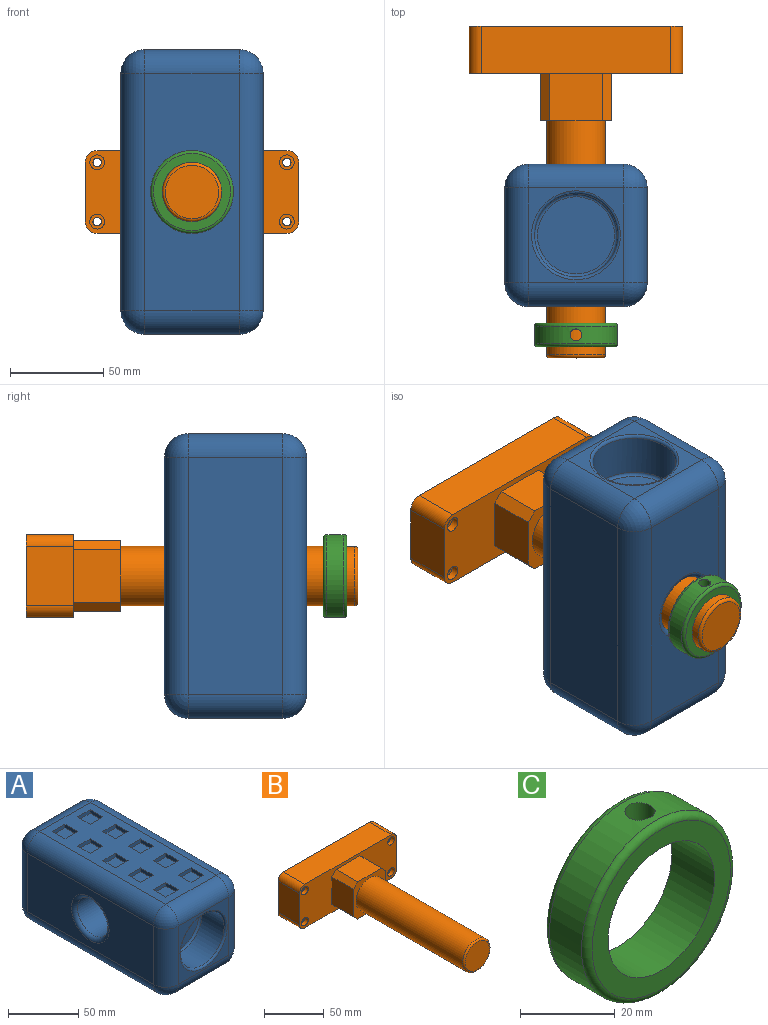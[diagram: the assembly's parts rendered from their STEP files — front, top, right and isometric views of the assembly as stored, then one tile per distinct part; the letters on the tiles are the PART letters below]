
ASSEMBLY  parts=3 mates=2
PART A: 87 faces, bbox 76.2x152.4x76.2 mm
  f0: plane 127x50.8mm, normal (0,0,1), area 4838.7mm2, adj f6,f10,f11,f12,f37,f38,f39,f40
  f1: plane 127x50.8mm, normal (0,0,-1), area 6451.6mm2, adj f14,f19,f22,f25
  f2: plane 127x50.8mm, normal (1,0,0), area 5311.5mm2, adj f11,f20,f21,f25,f36
  f3: plane 127x50.8mm, normal (-1,0,0), area 5311.5mm2, adj f6,f9,f13,f14,f35
  f4: plane 50.8x50.8mm, normal (0,-1,0), area 799.2mm2, adj f9,f10,f19,f20,f28
  f5: plane 50.8x50.8mm, normal (0,1,0), area 799.2mm2, adj f12,f13,f21,f22,f32
  f6: cylinder r=12.7mm len=127mm, axis (0,1,0), area 2533.5mm2, adj f0,f3,f7,f8
  f7: sphere r=12.7mm, area 253.4mm2, adj f6,f9,f10
  f8: sphere r=12.7mm, area 253.4mm2, adj f6,f12,f13
  f9: cylinder r=12.7mm len=50.8mm, axis (0,0,1), area 1013.4mm2, adj f3,f4,f7,f15
  f10: cylinder r=12.7mm len=50.8mm, axis (1,0,0), area 1013.4mm2, adj f0,f4,f7,f16
  f11: cylinder r=12.7mm len=127mm, axis (0,-1,0), area 2533.5mm2, adj f0,f2,f16,f17
  f12: cylinder r=12.7mm len=50.8mm, axis (-1,0,0), area 1013.4mm2, adj f0,f5,f8,f17
  f13: cylinder r=12.7mm len=50.8mm, axis (0,0,-1), area 1013.4mm2, adj f3,f5,f8,f18
  f14: cylinder r=12.7mm len=127mm, axis (0,-1,0), area 2533.5mm2, adj f1,f3,f15,f18
  f15: sphere r=12.7mm, area 253.4mm2, adj f9,f14,f19
  f16: sphere r=12.7mm, area 253.4mm2, adj f10,f11,f20
  f17: sphere r=12.7mm, area 253.4mm2, adj f11,f12,f21
  f18: sphere r=12.7mm, area 253.4mm2, adj f13,f14,f22
  f19: cylinder r=12.7mm len=50.8mm, axis (-1,0,0), area 1013.4mm2, adj f1,f4,f15,f23
  f20: cylinder r=12.7mm len=50.8mm, axis (0,0,-1), area 1013.4mm2, adj f2,f4,f16,f23
  f21: cylinder r=12.7mm len=50.8mm, axis (0,0,1), area 1013.4mm2, adj f2,f5,f17,f24
  f22: cylinder r=12.7mm len=50.8mm, axis (1,0,0), area 1013.4mm2, adj f1,f5,f18,f24
  f23: sphere r=12.7mm, area 253.4mm2, adj f19,f20,f25
  f24: sphere r=12.7mm, area 253.4mm2, adj f21,f22,f25
  f25: cylinder r=12.7mm len=127mm, axis (0,1,0), area 2533.5mm2, adj f1,f2,f23,f24
  f26: cylinder r=22.23mm len=44.45mm, axis (0,-1,0), area 3103.6mm2, adj f28,f29
  f27: plane 41.28x41.28mm, normal (0,-1,0), area 1338mm2, adj f29
  f28: torus R=23.81mm, axis (0,-1,0), area 357.3mm2, adj f4,f26
  f29: torus R=20.64mm, axis (0,-1,0), area 339.2mm2, adj f26,f27
  f30: cylinder r=22.23mm len=44.45mm, axis (0,1,0), area 3103.6mm2, adj f32,f33
  f31: plane 41.28x41.28mm, normal (0,1,0), area 1338mm2, adj f33
  f32: torus R=23.81mm, axis (0,-1,0), area 357.3mm2, adj f5,f30
  f33: torus R=20.64mm, axis (0,1,0), area 339.2mm2, adj f30,f31
  f34: cylinder r=15.88mm len=69.85mm, axis (1,0,0), area 6967.2mm2, adj f35,f36
  f35: torus R=19.05mm, axis (1,0,0), area 533.6mm2, adj f3,f34
  f36: torus R=19.05mm, axis (1,0,0), area 533.6mm2, adj f2,f34
  f37: plane 12.7x3.18mm, normal (0,-1,0), area 40.3mm2, adj f0,f38,f40,f41
  f38: plane 12.7x3.18mm, normal (1,0,0), area 40.3mm2, adj f0,f37,f39,f41
  f39: plane 12.7x3.18mm, normal (0,1,0), area 40.3mm2, adj f0,f38,f40,f41
  f40: plane 12.7x3.18mm, normal (-1,0,0), area 40.3mm2, adj f0,f37,f39,f41
  f41: plane 12.7x12.7mm, normal (0,0,1), area 161.3mm2, adj f37,f38,f39,f40
  f42: plane 12.7x3.18mm, normal (0,-1,0), area 40.3mm2, adj f0,f43,f45,f46
  f43: plane 12.7x3.18mm, normal (1,0,0), area 40.3mm2, adj f0,f42,f44,f46
  f44: plane 12.7x3.18mm, normal (0,1,0), area 40.3mm2, adj f0,f43,f45,f46
  f45: plane 12.7x3.18mm, normal (-1,0,0), area 40.3mm2, adj f0,f42,f44,f46
  f46: plane 12.7x12.7mm, normal (0,0,1), area 161.3mm2, adj f42,f43,f44,f45
  f47: plane 12.7x3.18mm, normal (0,-1,0), area 40.3mm2, adj f0,f48,f50,f51
  f48: plane 12.7x3.18mm, normal (1,0,0), area 40.3mm2, adj f0,f47,f49,f51
  f49: plane 12.7x3.18mm, normal (0,1,0), area 40.3mm2, adj f0,f48,f50,f51
  f50: plane 12.7x3.18mm, normal (-1,0,0), area 40.3mm2, adj f0,f47,f49,f51
  f51: plane 12.7x12.7mm, normal (0,0,1), area 161.3mm2, adj f47,f48,f49,f50
  f52: plane 12.7x3.18mm, normal (0,-1,0), area 40.3mm2, adj f0,f53,f55,f56
  f53: plane 12.7x3.18mm, normal (1,0,0), area 40.3mm2, adj f0,f52,f54,f56
  f54: plane 12.7x3.18mm, normal (0,1,0), area 40.3mm2, adj f0,f53,f55,f56
  f55: plane 12.7x3.18mm, normal (-1,0,0), area 40.3mm2, adj f0,f52,f54,f56
  f56: plane 12.7x12.7mm, normal (0,0,1), area 161.3mm2, adj f52,f53,f54,f55
  f57: plane 12.7x3.18mm, normal (0,-1,0), area 40.3mm2, adj f0,f58,f60,f61
  f58: plane 12.7x3.18mm, normal (1,0,0), area 40.3mm2, adj f0,f57,f59,f61
  f59: plane 12.7x3.18mm, normal (0,1,0), area 40.3mm2, adj f0,f58,f60,f61
  f60: plane 12.7x3.18mm, normal (-1,0,0), area 40.3mm2, adj f0,f57,f59,f61
  f61: plane 12.7x12.7mm, normal (0,0,1), area 161.3mm2, adj f57,f58,f59,f60
  f62: plane 12.7x3.18mm, normal (0,-1,0), area 40.3mm2, adj f0,f63,f65,f66
  f63: plane 12.7x3.18mm, normal (1,0,0), area 40.3mm2, adj f0,f62,f64,f66
  f64: plane 12.7x3.18mm, normal (0,1,0), area 40.3mm2, adj f0,f63,f65,f66
  f65: plane 12.7x3.18mm, normal (-1,0,0), area 40.3mm2, adj f0,f62,f64,f66
  f66: plane 12.7x12.7mm, normal (0,0,1), area 161.3mm2, adj f62,f63,f64,f65
  f67: plane 12.7x3.18mm, normal (0,-1,0), area 40.3mm2, adj f0,f68,f70,f71
  f68: plane 12.7x3.18mm, normal (1,0,0), area 40.3mm2, adj f0,f67,f69,f71
  f69: plane 12.7x3.18mm, normal (0,1,0), area 40.3mm2, adj f0,f68,f70,f71
  f70: plane 12.7x3.18mm, normal (-1,0,0), area 40.3mm2, adj f0,f67,f69,f71
  f71: plane 12.7x12.7mm, normal (0,0,1), area 161.3mm2, adj f67,f68,f69,f70
  f72: plane 12.7x3.18mm, normal (0,-1,0), area 40.3mm2, adj f0,f73,f75,f76
  f73: plane 12.7x3.18mm, normal (1,0,0), area 40.3mm2, adj f0,f72,f74,f76
  f74: plane 12.7x3.18mm, normal (0,1,0), area 40.3mm2, adj f0,f73,f75,f76
  f75: plane 12.7x3.18mm, normal (-1,0,0), area 40.3mm2, adj f0,f72,f74,f76
  f76: plane 12.7x12.7mm, normal (0,0,1), area 161.3mm2, adj f72,f73,f74,f75
  f77: plane 12.7x3.18mm, normal (0,-1,0), area 40.3mm2, adj f0,f78,f80,f81
  f78: plane 12.7x3.18mm, normal (1,0,0), area 40.3mm2, adj f0,f77,f79,f81
  f79: plane 12.7x3.18mm, normal (0,1,0), area 40.3mm2, adj f0,f78,f80,f81
  f80: plane 12.7x3.18mm, normal (-1,0,0), area 40.3mm2, adj f0,f77,f79,f81
  f81: plane 12.7x12.7mm, normal (0,0,1), area 161.3mm2, adj f77,f78,f79,f80
  f82: plane 12.7x3.18mm, normal (0,-1,0), area 40.3mm2, adj f0,f83,f85,f86
  f83: plane 12.7x3.18mm, normal (1,0,0), area 40.3mm2, adj f0,f82,f84,f86
  f84: plane 12.7x3.18mm, normal (0,1,0), area 40.3mm2, adj f0,f83,f85,f86
  f85: plane 12.7x3.18mm, normal (-1,0,0), area 40.3mm2, adj f0,f82,f84,f86
  f86: plane 12.7x12.7mm, normal (0,0,1), area 161.3mm2, adj f82,f83,f84,f85
PART B: 34 faces, bbox 114.3x177.8x44.5 mm
  f0: cylinder r=15.86mm len=125.41mm, axis (0,1,0), area 12499.3mm2, adj f2,f7
  f1: plane 28.55x28.55mm, normal (0,-1,0), area 640.2mm2, adj f2
  f2: torus R=14.27mm, axis (0,-1,0), area 239.5mm2, adj f0,f1
  f3: plane 27.94x25.4mm, normal (1,0,0), area 709.7mm2, adj f7,f9,f10,f12
  f4: plane 27.94x25.4mm, normal (0,0,1), area 709.7mm2, adj f7,f10,f11,f12
  f5: plane 27.94x25.4mm, normal (-1,0,0), area 709.7mm2, adj f7,f8,f11,f12
  f6: plane 27.94x25.4mm, normal (0,0,-1), area 709.7mm2, adj f7,f8,f9,f12
  f7: plane 38.1x38.1mm, normal (0,-1,0), area 609.5mm2, adj f0,f3,f4,f5,f6,f8,f9,f10
  f8: plane 25.4x5.08mm, normal (-0.71,0,-0.71), area 182.5mm2, adj f5,f6,f7,f12
  f9: plane 25.4x5.08mm, normal (0.71,0,-0.71), area 182.5mm2, adj f3,f6,f7,f12
  f10: plane 25.4x5.08mm, normal (0.71,0,0.71), area 182.5mm2, adj f3,f4,f7,f12
  f11: plane 25.4x5.08mm, normal (-0.71,0,0.71), area 182.5mm2, adj f4,f5,f7,f12
  f12: plane 114.3x44.45mm, normal (0,-1,0), area 3448.1mm2, adj f3,f4,f5,f6,f8,f9,f10,f11
  f13: plane 31.75x25.4mm, normal (-1,0,0), area 806.5mm2, adj f12,f14,f20,f21
  f14: cylinder r=6.35mm len=25.4mm, axis (0,-1,0), area 253.4mm2, adj f12,f13,f15,f21
  f15: plane 101.6x25.4mm, normal (0,0,1), area 2580.6mm2, adj f12,f14,f16,f21
  f16: cylinder r=6.35mm len=25.4mm, axis (0,-1,0), area 253.4mm2, adj f12,f15,f17,f21
  f17: plane 31.75x25.4mm, normal (1,0,0), area 806.5mm2, adj f12,f16,f18,f21
  f18: cylinder r=6.35mm len=25.4mm, axis (0,-1,0), area 253.4mm2, adj f12,f17,f19,f21
  f19: plane 101.6x25.4mm, normal (0,0,-1), area 2580.6mm2, adj f12,f18,f20,f21
  f20: cylinder r=6.35mm len=25.4mm, axis (0,-1,0), area 253.4mm2, adj f12,f13,f19,f21
  f21: plane 114.3x44.45mm, normal (0,1,0), area 4982.5mm2, adj f13,f14,f15,f16,f17,f18,f19,f20
  f22: cylinder r=2.25mm len=21.23mm, axis (0,-1,0), area 299.9mm2, adj f21,f23
  f23: plane 7.94x7.94mm, normal (0,-1,0), area 33.6mm2, adj f22,f24
  f24: cylinder r=3.97mm len=7.94mm, axis (0,-1,0), area 103.9mm2, adj f12,f23
  f25: cylinder r=2.25mm len=21.23mm, axis (0,-1,0), area 299.9mm2, adj f21,f26
  f26: plane 7.94x7.94mm, normal (0,-1,0), area 33.6mm2, adj f25,f27
  f27: cylinder r=3.97mm len=7.94mm, axis (0,-1,0), area 103.9mm2, adj f12,f26
  f28: cylinder r=2.25mm len=21.23mm, axis (0,-1,0), area 299.9mm2, adj f21,f29
  f29: plane 7.94x7.94mm, normal (0,-1,0), area 33.6mm2, adj f28,f30
  f30: cylinder r=3.97mm len=7.94mm, axis (0,-1,0), area 103.9mm2, adj f12,f29
  f31: cylinder r=2.25mm len=21.23mm, axis (0,-1,0), area 299.9mm2, adj f21,f32
  f32: plane 7.94x7.94mm, normal (0,-1,0), area 33.6mm2, adj f31,f33
  f33: cylinder r=3.97mm len=7.94mm, axis (0,-1,0), area 103.9mm2, adj f12,f32
PART C: 7 faces, bbox 48.1x12.7x48.1 mm
  f0: cylinder r=15.88mm len=31.75mm, axis (0,1,0), area 1235.2mm2, adj f2,f3,f4
  f1: cylinder r=22.23mm len=44.45mm, axis (0,1,0), area 1298.5mm2, adj f4,f5,f6
  f2: plane 41.28x41.28mm, normal (0,-1,0), area 546.3mm2, adj f0,f6
  f3: plane 41.28x41.28mm, normal (0,1,0), area 546.3mm2, adj f0,f5
  f4: cylinder r=3.17mm len=6.67mm, axis (0,0,1), area 127.6mm2, adj f0,f1
  f5: torus R=20.64mm, axis (0,-1,0), area 339.2mm2, adj f1,f3
  f6: torus R=20.64mm, axis (0,-1,0), area 339.2mm2, adj f1,f2
PLACE A rot(axis=(0.58,0.58,0.58),120deg) t=(-111.21,-57.13,109.38)mm
PLACE B t=(-111.21,4.28,33.18)mm
PLACE C t=(-111.21,-104.05,33.18)mm
MATE cylindrical C.f0 <-> B.f0  axis (0,1,0) through (-111.21,-116.75,33.18)mm
MATE cylindrical A.f36 <-> B.f0  axis (0,1,0) through (-111.21,-22.2,33.18)mm
